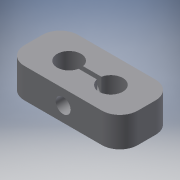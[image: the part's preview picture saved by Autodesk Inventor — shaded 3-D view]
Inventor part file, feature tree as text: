
AUTODESK INVENTOR PART (.ipt)
format: ipt  version: 2017 SP1 (Build 210196100, 196)  size: 142,848 bytes
history: native  units: mm
features: extrude x4, sketch x3, fillet x1, projected_geometry x1
ambient origin geometry x8: Origin, YZ Plane, XZ Plane, XY Plane, X Axis, Y Axis, Z Axis, Center Point
bodies: Solid1 (feature_tree)
feature tree (9):
  extrude  "Extrusion1"  Depth=14.0mm
  extrude  "Extrusion2"  Depth=18.0mm
  fillet  "Fillet1"  Radius=10.0mm
  extrude  "Extrusion3"  Depth=10.0mm TaperAngle=0.0deg
  extrude  "Extrusion4"  Depth=6.0mm
  sketch  "Sketch1"  dims[d0=8.0mm d1=14.0mm]
  sketch  "Sketch3"  dims[d2=12.0mm d3=18.0mm d4=10.0mm d5=0.0mm]
  sketch  "Sketch4"  dims[d6=5.0mm d7=8.0mm d8=0.0mm d9=6.0mm d10=1.5mm d11=8.0mm d12=0.0mm d13=38.0mm d14=9.525mm d15=10.0mm d16=0.0mm d17=19.0mm]
  projected_geometry  "Projected Loop1"
